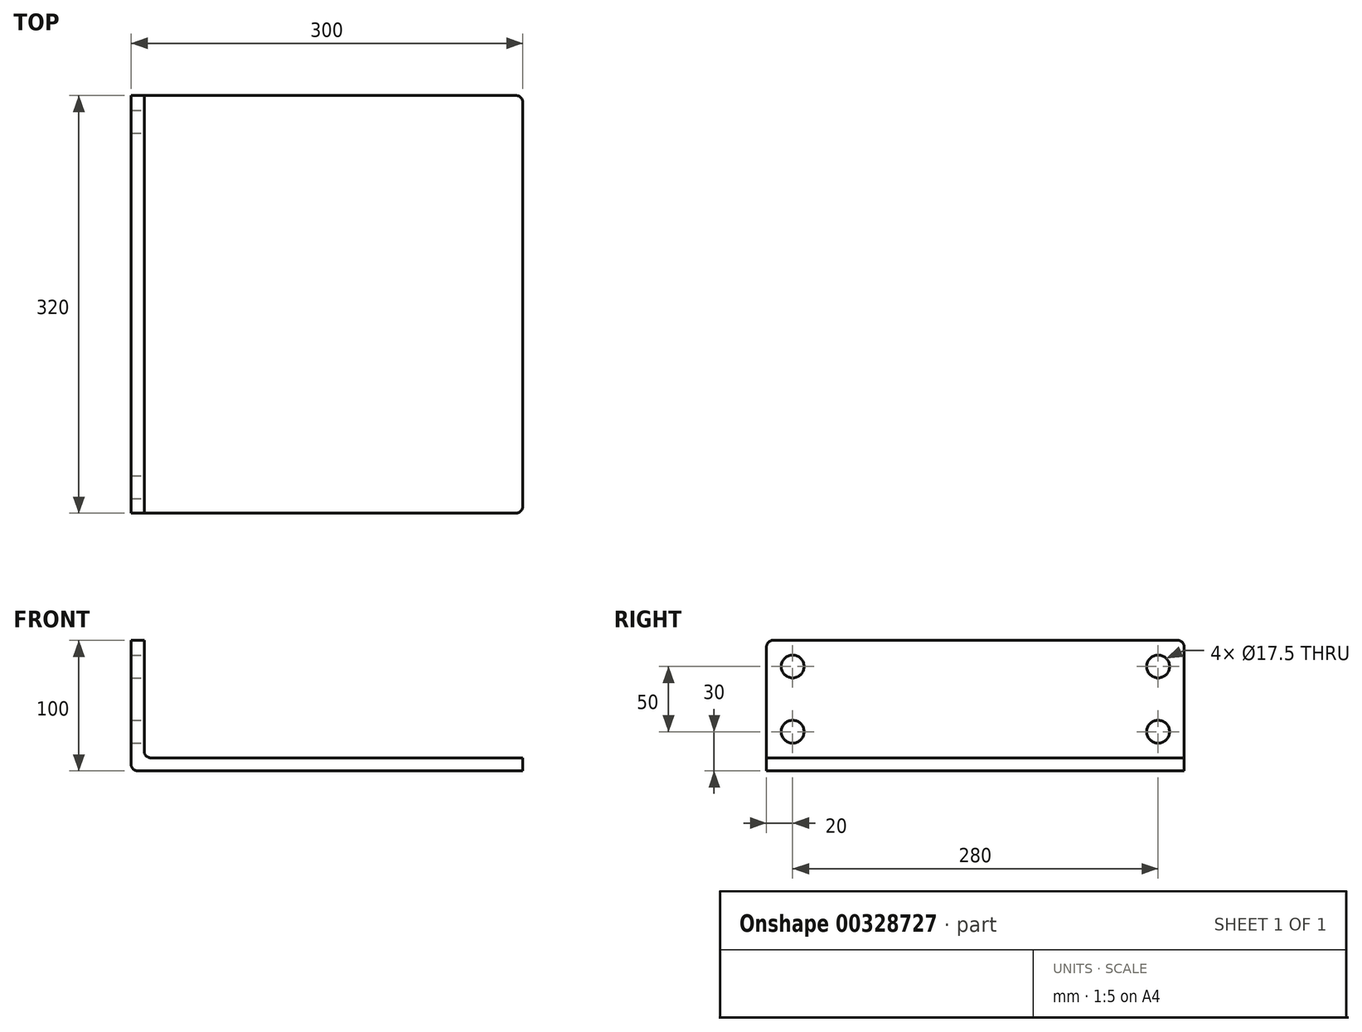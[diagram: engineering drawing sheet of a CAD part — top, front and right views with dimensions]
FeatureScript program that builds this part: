
annotation { "Feature Type Name" : "Feature", "Feature Type Description" : "" }
export const myFeature = defineFeature(function(context is Context, id is Id, definition is map)
    precondition{}
    {
        {
            var Q0;
            Q0=qCreatedBy(makeId("Front.planeOp"),FACE);
            var sketch = newSketch(context, id + "F0", { "sketchPlane" : qUnion([Q0])});
            skLineSegment(sketch, "E0.bottom", {"start": v(0, 0) * mm, "end": v(0, 0) * mm});
            skLineSegment(sketch, "E0.top", {"start": v(0, -24.55) * mm, "end": v(0, -24.55) * mm});
            skLineSegment(sketch, "E1.top", {"start": v(5, 45) * mm, "end": v(-5, 45) * mm});
            skLineSegment(sketch, "E1.left", {"start": v(5, -45) * mm, "end": v(5, 45) * mm});
            skLineSegment(sketch, "E1.right", {"start": v(-5, -45) * mm, "end": v(-5, 45) * mm});
            skPoint(sketch, "E1.middle", {"position": v(0, 0) * mm});
            skLineSegment(sketch, "E2.bottom", {"start": v(5, -45) * mm, "end": v(295, -45) * mm});
            skLineSegment(sketch, "E2.top", {"start": v(-5, -55) * mm, "end": v(295, -55) * mm});
            skLineSegment(sketch, "E2.left", {"start": v(-5, -45) * mm, "end": v(-5, -55) * mm});
            skLineSegment(sketch, "E2.right", {"start": v(295, -45) * mm, "end": v(295, -55) * mm});
            skSolve(sketch);
        }
        {
            var Q0;
            Q0=makeQuery(id+"F0.imprint","IMPRINT",FACE,{"disambiguationData":[TD([[makeQuery(id+"F0.imprint","IMPRINT",EDGE,{"derivedFrom":sQuery(id+"F0.wireOp",EDGE,"E1.top")}),1.0]])]});
            extrude(context, id + "F1", {"entities" : qUnion([Q0]), "oppositeDirection" : true, "depth" : 320 * mm});
        }
        {
            var Q0;
            Q0=makeQuery(id+"F1.opExtrude","CAP_EDGE",EDGE,{"disambiguationData":[OSD([sQuery(id+"F0.wireOp",EDGE,"E1.top")])],"isStart":true});
            var Q1;
            Q1=makeQuery(id+"F1.opExtrude","CAP_EDGE",EDGE,{"disambiguationData":[OSD([sQuery(id+"F0.wireOp",EDGE,"E1.top")])],"isStart":false});
            var Q2;
            Q2=makeQuery(id+"F1.opExtrude","CAP_EDGE",EDGE,{"disambiguationData":[OSD([sQuery(id+"F0.wireOp",EDGE,"E2.right")])],"isStart":false});
            var Q3;
            Q3=makeQuery(id+"F1.opExtrude","CAP_EDGE",EDGE,{"disambiguationData":[OSD([sQuery(id+"F0.wireOp",EDGE,"E2.right")])],"isStart":true});
            fillet(context, id + "F2", {"entities" : qUnion([Q0, Q1, Q2, Q3]), "radius" : 5 * mm, "tangentPropagation" : true, "allowEdgeOverflow" : false});
        }
        {
            var Q0;
            Q0=makeQuery(id+"F1.opExtrude","SWEPT_FACE",FACE,{"disambiguationData":[OSD([sQuery(id+"F0.wireOp",EDGE,"E1.left")])]});
            var sketch = newSketch(context, id + "F3", { "sketchPlane" : qUnion([Q0])});
            skCircle(sketch, "E3", {"center": v(20, 25) * mm, "radius": 8 * mm});
            skCircle(sketch, "E4", {"center": v(20, -25) * mm, "radius": 8 * mm});
            skCircle(sketch, "E5", {"center": v(300, -25) * mm, "radius": 8 * mm});
            skCircle(sketch, "E6", {"center": v(300, 25) * mm, "radius": 8 * mm});
            skSolve(sketch);
        }
        {
            var Q0;
            Q0=sQuery(id+"F3.wireOp",VERTEX,"E4.center");
            var Q1;
            Q1=sQuery(id+"F3.wireOp",VERTEX,"E3.center");
            var Q2;
            Q2=sQuery(id+"F3.wireOp",VERTEX,"E6.center");
            var Q3;
            Q3=sQuery(id+"F3.wireOp",VERTEX,"E5.center");
            var Q4;
            Q4=makeQuery(id+"F1.opExtrude","SWEPT_BODY",BODY,{"disambiguationData":[OSD([sQuery(id+"F0.wireOp",EDGE,"E1.top"),sQuery(id+"F0.wireOp",EDGE,"E1.left"),sQuery(id+"F0.wireOp",EDGE,"E1.right"),sQuery(id+"F0.wireOp",EDGE,"E2.bottom"),sQuery(id+"F0.wireOp",EDGE,"E2.top"),sQuery(id+"F0.wireOp",EDGE,"E2.left"),sQuery(id+"F0.wireOp",EDGE,"E2.right")])]});
            hole(context, id + "F4", {"style" : HoleStyle.SIMPLE, "endStyle" : HoleEndStyle.BLIND, "standardTappedOrClearance" : lookupTablePath({ "standard" : "ISO", "fit" : "Normal", "size" : "M16", "type" : "Clearance" }), "standardBlindInLast" : lookupTablePath({ "fit" : "Standard", "standard" : "ISO", "size" : "M16", "type" : "Clearance" }), "holeDiameter" : 17.5 * mm, "holeDepth" : 20 * mm, "tappedDepth" : 14 * mm, "tapClearance" : 3, "locations" : qUnion([Q0, Q1, Q2, Q3]), "scope" : qUnion([Q4])});
        }
        {
            var Q0;
            Q0=makeQuery(id+"F1.opExtrude","SWEPT_EDGE",EDGE,{"disambiguationData":[OSD([sQuery(id+"F0.wireOp",EDGE,"E2.top"),sQuery(id+"F0.wireOp",EDGE,"E2.left")])]});
            fillet(context, id + "F5", {"entities" : qUnion([Q0]), "radius" : 5 * mm, "tangentPropagation" : true, "allowEdgeOverflow" : false});
        }
        {
            var Q0;
            Q0=makeQuery(id+"F1.opExtrude","SWEPT_EDGE",EDGE,{"disambiguationData":[OSD([sQuery(id+"F0.wireOp",EDGE,"E1.left"),sQuery(id+"F0.wireOp",EDGE,"E2.bottom")])]});
            fillet(context, id + "F6", {"entities" : qUnion([Q0]), "radius" : 5 * mm, "tangentPropagation" : true, "allowEdgeOverflow" : false});
        }
    });
